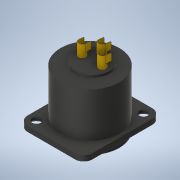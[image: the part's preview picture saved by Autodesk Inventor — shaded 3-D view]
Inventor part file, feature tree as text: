
AUTODESK INVENTOR PART (.ipt)
format: ipt  version: 2020.1 (Build 241239000, 239)  size: 1,619,456 bytes
history: native  units: mm
features: other x12, surface_op x7, sketch x4, extrude x1
ambient origin geometry x8: Origin, YZ Plane, XZ Plane, XY Plane, X Axis, Y Axis, Z Axis, Center Point
bodies: Solid1 (feature_tree), Solid2 (feature_tree), Solid3 (feature_tree), Solid4 (feature_tree), Solid5 (feature_tree)
feature tree (24):
  surface_op  "Sculpt1"
  extrude  "Extrusion1"  TaperAngle=0.0deg  [1 undecoded]
  sketch  "Sketch2"  dims[d2=5.0mm]
  sketch  "Sketch3"  dims[d3=0.0mm]
  sketch  "Sketch4"  dims[d4=5.0mm d5=0.0mm d6=5.0mm d7=0.0mm d8=5.0mm d9=0.0mm d10=5.0mm d11=0.0mm d12=25.4mm d13=0.0mm d14=2.54mm]
  other  "Srf3"
  other  "Srf4"
  other  "Srf5"
  other  "Srf6"
  other  "Srf7"
  other  "Srf8"
  sketch  "Sketch1"  dims[d0=5.0mm d1=0.0mm]
  other  "push button"
  other  "brep_2"
  other  "brep_3"
  other  "brep_4"
  other  "Composite1"
  other  "Srf1"
  surface_op  "Boundary Patch1"
  surface_op  "Boundary Patch2"
  surface_op  "Boundary Patch3"
  surface_op  "Boundary Patch4"
  surface_op  "Boundary Patch5"
  surface_op  "Boundary Patch6"
note: 1 required parameter value undecoded (feature->parameter linkage not recoverable at this tier; creation-order binding heuristic only, values carry confidence <= 0.55)
